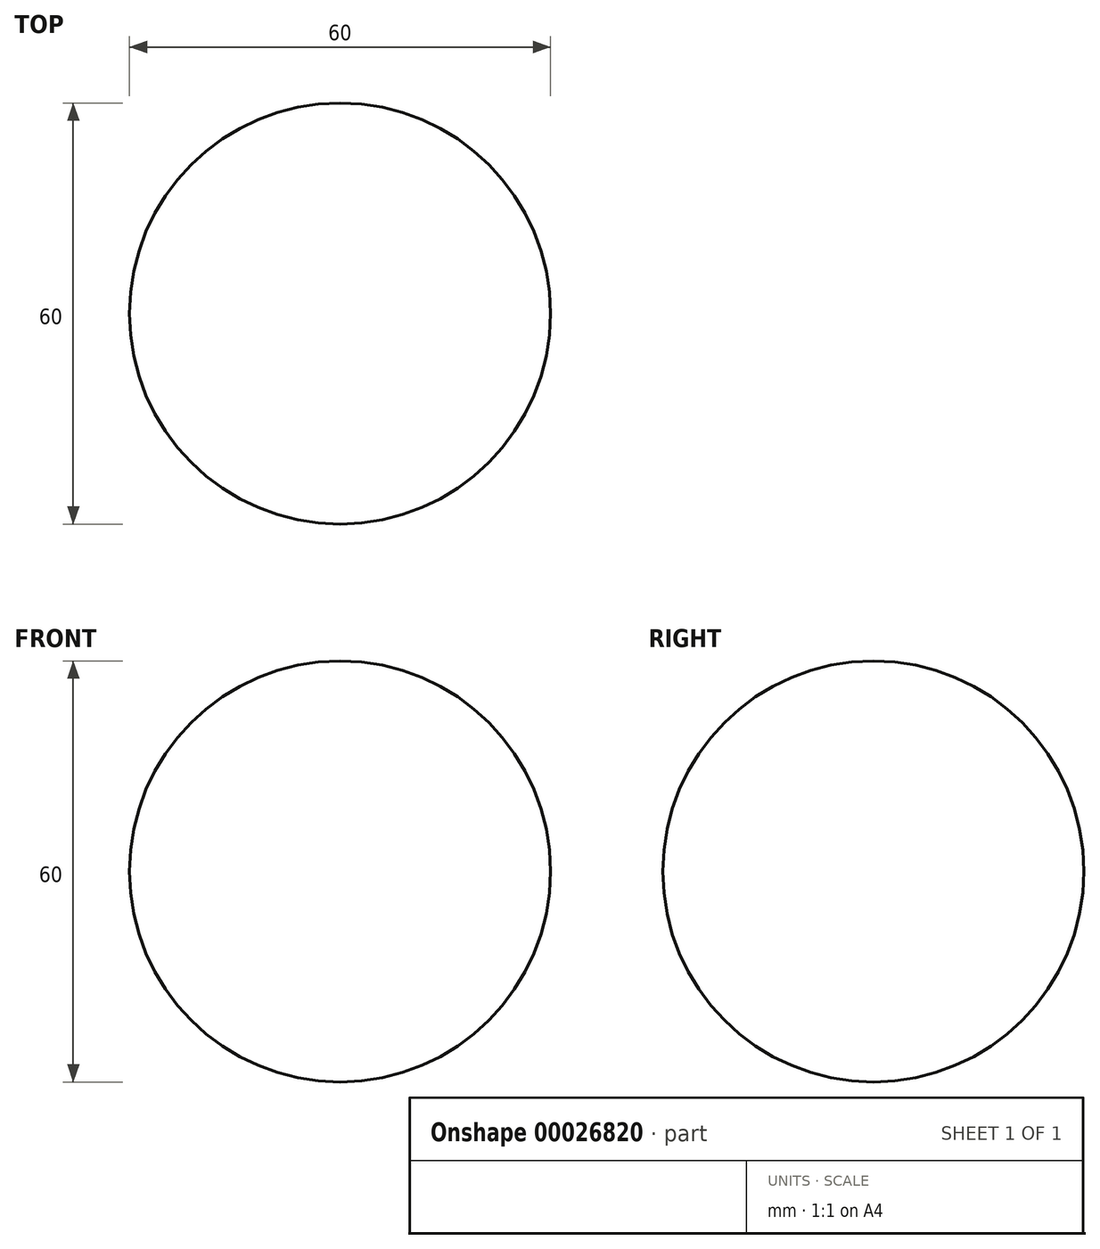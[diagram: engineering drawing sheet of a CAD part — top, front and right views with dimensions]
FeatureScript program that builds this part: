
annotation { "Feature Type Name" : "Feature", "Feature Type Description" : "" }
export const myFeature = defineFeature(function(context is Context, id is Id, definition is map)
    precondition{}
    {
        {
            var Q0;
            Q0=qCreatedBy(makeId("Top.planeOp"),FACE);
            var sketch = newSketch(context, id + "F0", { "sketchPlane" : qUnion([Q0])});
            skArc(sketch, "E0", {"start": v(0, -30) * mm, "mid": v(30, 0) * mm, "end": v(0, 30) * mm});
            skLineSegment(sketch, "E1", {"start": v(0, 30) * mm, "end": v(0, -30) * mm});
            skSolve(sketch);
        }
        {
            var Q0;
            Q0=makeQuery(id+"F0.imprint","IMPRINT",FACE,{"disambiguationData":[TD([[makeQuery(id+"F0.imprint","IMPRINT",EDGE,{"derivedFrom":sQuery(id+"F0.wireOp",EDGE,"E0")}),1.0]])]});
            var Q1;
            Q1=sQuery(id+"F0.wireOp",EDGE,"E1");
            revolve(context, id + "F1", {"entities" : qUnion([Q0]), "axis" : qUnion([Q1]), "revolveType" : RevolveType.FULL});
        }
    });
